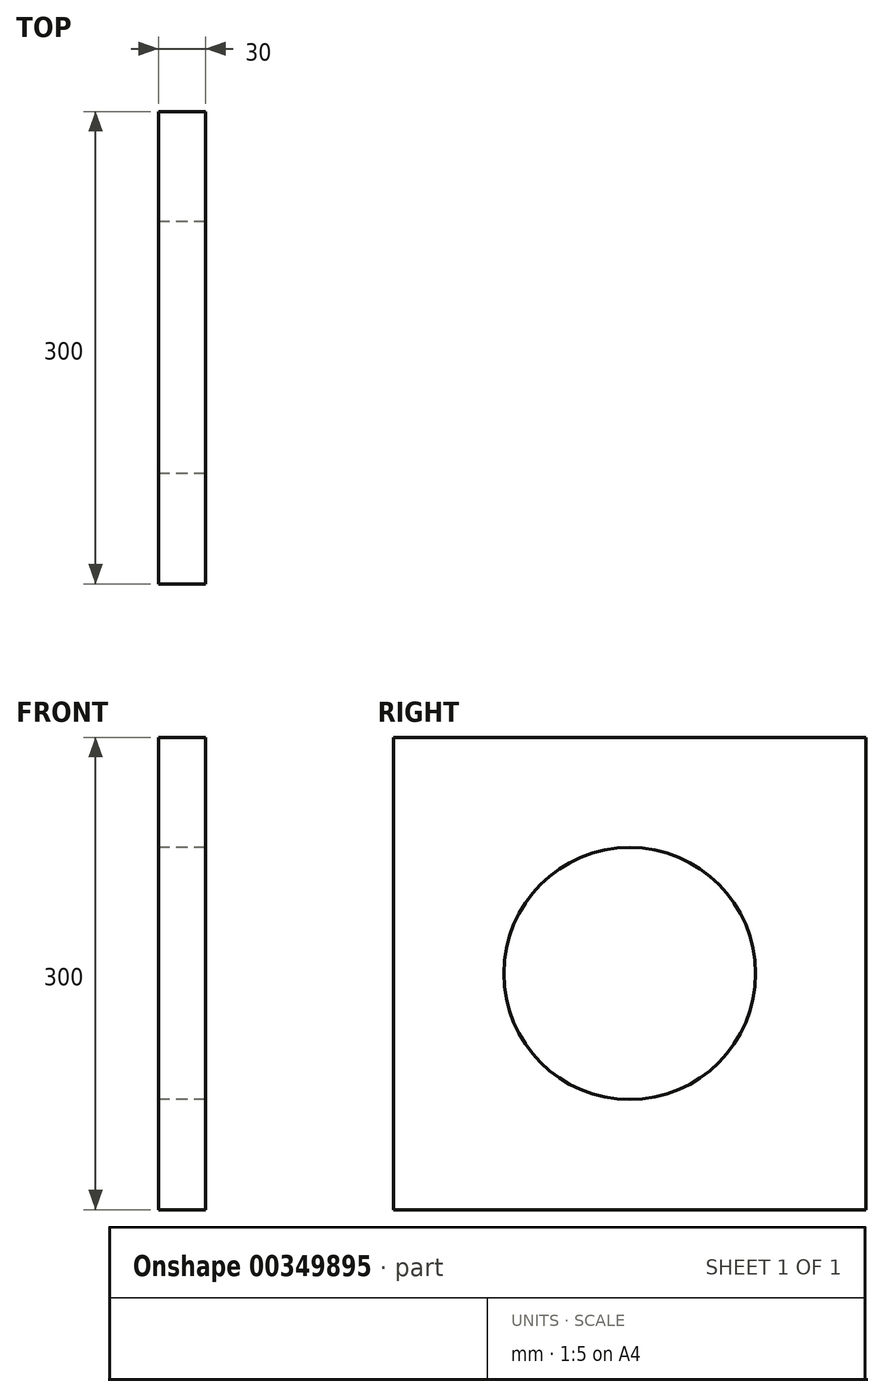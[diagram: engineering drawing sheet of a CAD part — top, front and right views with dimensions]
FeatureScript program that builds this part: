
annotation { "Feature Type Name" : "Feature", "Feature Type Description" : "" }
export const myFeature = defineFeature(function(context is Context, id is Id, definition is map)
    precondition{}
    {
        {
            var Q0;
            Q0=qCreatedBy(makeId("Right.planeOp"),FACE);
            var sketch = newSketch(context, id + "F0", { "sketchPlane" : qUnion([Q0])});
            skLineSegment(sketch, "E0.bottom", {"start": v(150, -150) * mm, "end": v(-150, -150) * mm});
            skLineSegment(sketch, "E0.top", {"start": v(150, 150) * mm, "end": v(-150, 150) * mm});
            skLineSegment(sketch, "E0.left", {"start": v(150, -150) * mm, "end": v(150, 150) * mm});
            skLineSegment(sketch, "E0.right", {"start": v(-150, -150) * mm, "end": v(-150, 150) * mm});
            skPoint(sketch, "E0.middle", {"position": v(0, 0) * mm});
            skCircle(sketch, "E1", {"center": v(0, 0) * mm, "radius": 80 * mm});
            skSolve(sketch);
        }
        {
            var Q0;
            Q0 = qSketchRegion(id + "F0", true);
            extrude(context, id + "F1", {"entities" : qUnion([Q0]), "depth" : 30 * mm});
        }
    });
